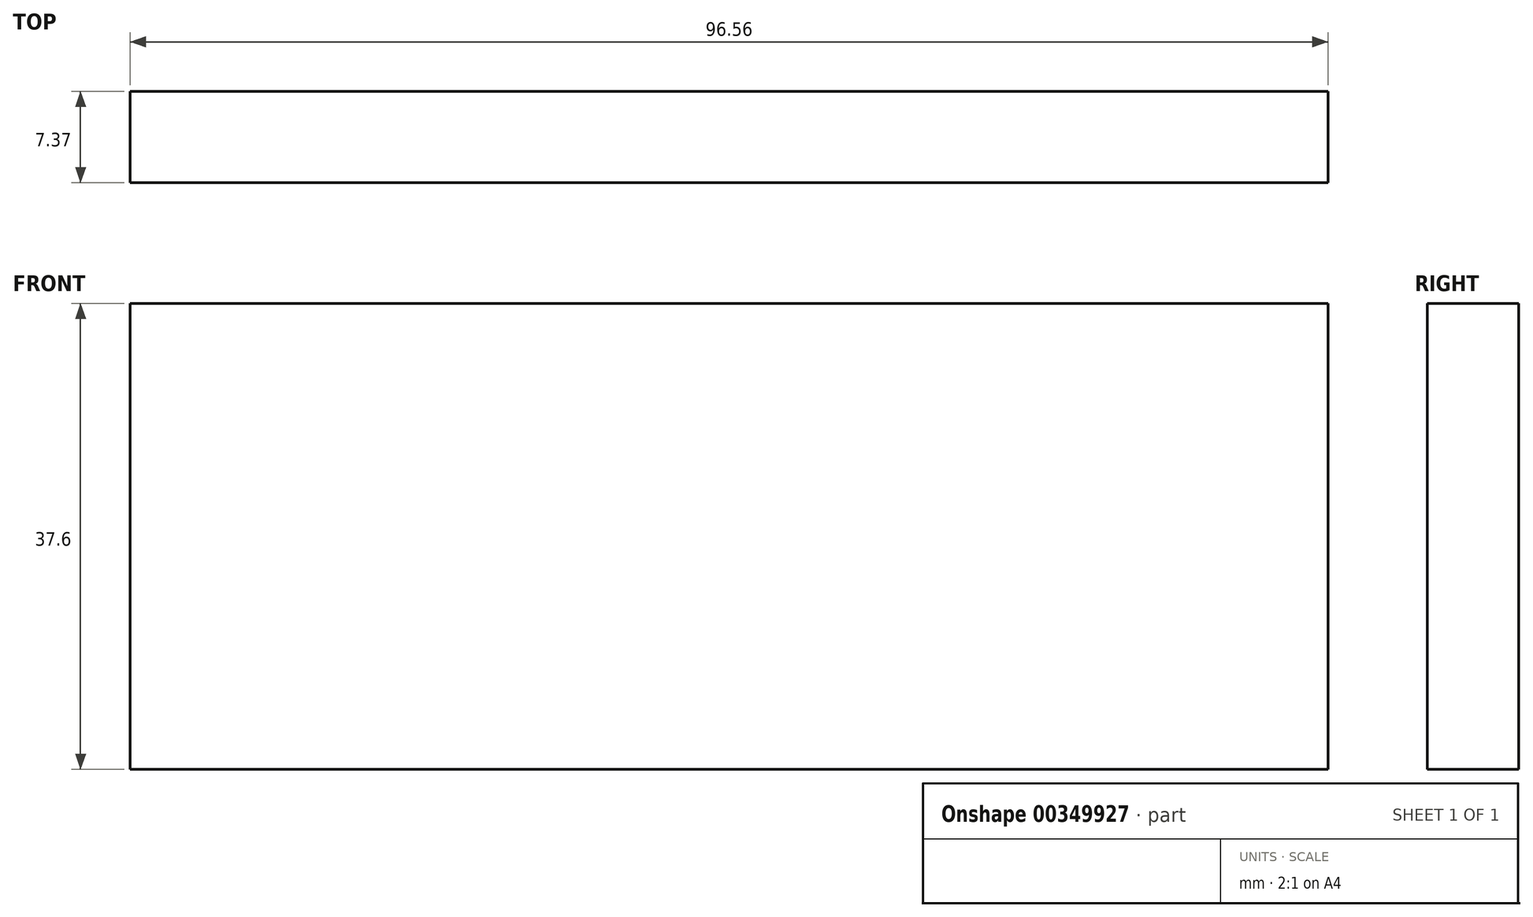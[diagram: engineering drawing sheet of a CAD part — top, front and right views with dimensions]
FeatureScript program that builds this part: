
annotation { "Feature Type Name" : "Feature", "Feature Type Description" : "" }
export const myFeature = defineFeature(function(context is Context, id is Id, definition is map)
    precondition{}
    {
        {
            var Q0;
            Q0=qCreatedBy(makeId("Front.planeOp"),FACE);
            var sketch = newSketch(context, id + "F0", { "sketchPlane" : qUnion([Q0])});
            skLineSegment(sketch, "E0.bottom", {"start": v(48.28, -18.8) * mm, "end": v(-48.28, -18.8) * mm});
            skLineSegment(sketch, "E0.top", {"start": v(48.28, 18.8) * mm, "end": v(-48.28, 18.8) * mm});
            skLineSegment(sketch, "E0.left", {"start": v(48.28, -18.8) * mm, "end": v(48.28, 18.8) * mm});
            skLineSegment(sketch, "E0.right", {"start": v(-48.28, -18.8) * mm, "end": v(-48.28, 18.8) * mm});
            skPoint(sketch, "E0.middle", {"position": v(0, 0) * mm});
            skSolve(sketch);
        }
        {
            var Q0;
            Q0 = qSketchRegion(id + "F0", true);
            extrude(context, id + "F1", {"entities" : qUnion([Q0]), "depth" : 7.37 * mm, "offsetDistance" : 25.4 * mm});
        }
    });
